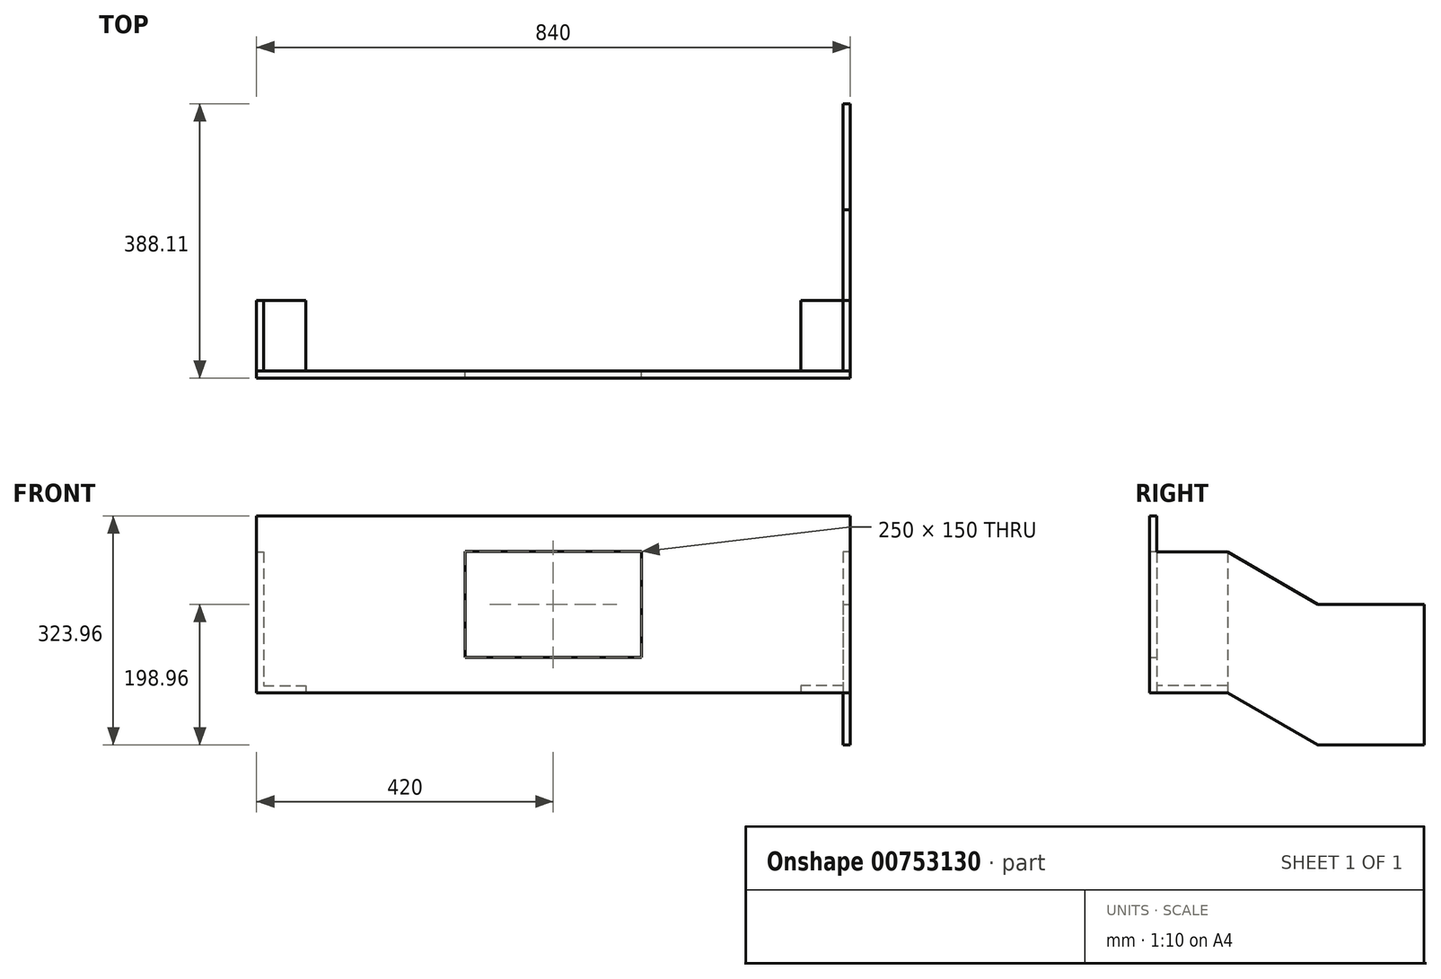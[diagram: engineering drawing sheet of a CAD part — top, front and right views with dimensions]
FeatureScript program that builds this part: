
annotation { "Feature Type Name" : "Feature", "Feature Type Description" : "" }
export const myFeature = defineFeature(function(context is Context, id is Id, definition is map)
    precondition{}
    {
        {
            var Q0;
            Q0=qCreatedBy(makeId("Front.planeOp"),FACE);
            var sketch = newSketch(context, id + "F0", { "sketchPlane" : qUnion([Q0])});
            skLineSegment(sketch, "E0.bottom", {"start": v(-420, 125) * mm, "end": v(420, 125) * mm});
            skLineSegment(sketch, "E0.top", {"start": v(-420, -125) * mm, "end": v(420, -125) * mm});
            skLineSegment(sketch, "E0.left", {"start": v(-420, 125) * mm, "end": v(-420, -125) * mm});
            skLineSegment(sketch, "E0.right", {"start": v(420, 125) * mm, "end": v(420, -125) * mm});
            skPoint(sketch, "E0.middle", {"position": v(0, 0) * mm});
            skLineSegment(sketch, "E1.bottom", {"start": v(-125, 75) * mm, "end": v(125, 75) * mm});
            skLineSegment(sketch, "E1.top", {"start": v(-125, -75) * mm, "end": v(125, -75) * mm});
            skLineSegment(sketch, "E1.left", {"start": v(-125, 75) * mm, "end": v(-125, -75) * mm});
            skLineSegment(sketch, "E1.right", {"start": v(125, 75) * mm, "end": v(125, -75) * mm});
            skSolve(sketch);
        }
        {
            var Q0;
            Q0=makeQuery(id+"F0.imprint","IMPRINT",FACE,{"disambiguationData":[TD([[makeQuery(id+"F0.imprint","IMPRINT",EDGE,{"derivedFrom":sQuery(id+"F0.wireOp",EDGE,"E0.bottom")}),-1.0]])]});
            extrude(context, id + "F1", {"entities" : qUnion([Q0]), "depth" : 10 * mm, "offsetDistance" : 25.4 * mm});
        }
        {
            var Q0;
            Q0=makeQuery(id+"F1.opExtrude","CAP_FACE",FACE,{"disambiguationData":[OSD([sQuery(id+"F0.wireOp",EDGE,"E0.bottom"),sQuery(id+"F0.wireOp",EDGE,"E0.top"),sQuery(id+"F0.wireOp",EDGE,"E0.left"),sQuery(id+"F0.wireOp",EDGE,"E0.right"),sQuery(id+"F0.wireOp",EDGE,"E1.bottom"),sQuery(id+"F0.wireOp",EDGE,"E1.top"),sQuery(id+"F0.wireOp",EDGE,"E1.left"),sQuery(id+"F0.wireOp",EDGE,"E1.right")])],"isStart":true});
            var sketch = newSketch(context, id + "F2", { "sketchPlane" : qUnion([Q0])});
            skLineSegment(sketch, "E2", {"start": v(-410, 73.96) * mm, "end": v(-410, -115) * mm});
            skLineSegment(sketch, "E3", {"start": v(-410, -115) * mm, "end": v(-350, -115) * mm});
            skLineSegment(sketch, "E4", {"start": v(-350, -115) * mm, "end": v(-350, -125) * mm});
            skLineSegment(sketch, "E5", {"start": v(-350, -125) * mm, "end": v(-420, -125) * mm});
            skLineSegment(sketch, "E6", {"start": v(-420, -125) * mm, "end": v(-420, 73.96) * mm});
            skLineSegment(sketch, "E7", {"start": v(-420, 73.96) * mm, "end": v(-410, 73.96) * mm});
            skLineSegment(sketch, "E8", {"start": v(420, 73.96) * mm, "end": v(410, 73.96) * mm});
            skLineSegment(sketch, "E9", {"start": v(410, 73.96) * mm, "end": v(410, -115) * mm});
            skLineSegment(sketch, "E10", {"start": v(410, -115) * mm, "end": v(350, -115) * mm});
            skLineSegment(sketch, "E11", {"start": v(350, -115) * mm, "end": v(350, -125) * mm});
            skLineSegment(sketch, "E12", {"start": v(350, -125) * mm, "end": v(420, -125) * mm});
            skLineSegment(sketch, "E13", {"start": v(420, -125) * mm, "end": v(420, 73.96) * mm});
            skSolve(sketch);
        }
        {
            var Q0;
            Q0=makeQuery(id+"F2.imprint","IMPRINT",FACE,{"disambiguationData":[TD([[makeQuery(id+"F2.imprint","IMPRINT",EDGE,{"derivedFrom":sQuery(id+"F2.wireOp",EDGE,"E8")}),1.0]])]});
            var Q1;
            Q1=makeQuery(id+"F2.imprint","IMPRINT",FACE,{"disambiguationData":[TD([[makeQuery(id+"F2.imprint","IMPRINT",EDGE,{"derivedFrom":sQuery(id+"F2.wireOp",EDGE,"E2")}),-1.0]])]});
            extrude(context, id + "F3", {"entities" : qUnion([Q0, Q1]), "operationType" : NewBodyOperationType.ADD, "depth" : 100 * mm, "offsetDistance" : 25.4 * mm});
        }
        {
            var Q0;
            Q0=makeQuery(id+"F3.boolean.opBoolean","MERGE",FACE,{"derivedFrom":[makeQuery(id+"F1.opExtrude","SWEPT_FACE",FACE,{"disambiguationData":[OSD([sQuery(id+"F0.wireOp",EDGE,"E0.right")])]}),makeQuery(id+"F3.opExtrude","SWEPT_FACE",FACE,{"disambiguationData":[OSD([sQuery(id+"F2.wireOp",EDGE,"E6")])]})]});
            var sketch = newSketch(context, id + "F4", { "sketchPlane" : qUnion([Q0])});
            skLineSegment(sketch, "E14", {"start": v(100, 73.96) * mm, "end": v(228.1, 0) * mm});
            skLineSegment(sketch, "E15", {"start": v(228.1, 0) * mm, "end": v(228.1, -198.96) * mm});
            skLineSegment(sketch, "E16", {"start": v(228.1, -198.96) * mm, "end": v(100, -125) * mm});
            skLineSegment(sketch, "E17", {"start": v(100, -125) * mm, "end": v(100, 73.96) * mm});
            skLineSegment(sketch, "E18", {"start": v(228.1, 0) * mm, "end": v(378.1, 0) * mm});
            skLineSegment(sketch, "E19", {"start": v(378.1, 0) * mm, "end": v(378.1, -198.96) * mm});
            skLineSegment(sketch, "E20", {"start": v(378.1, -198.96) * mm, "end": v(228.1, -198.96) * mm});
            skSolve(sketch);
        }
        {
            var Q0;
            Q0=makeQuery(id+"F4.imprint","IMPRINT",FACE,{"disambiguationData":[TD([[makeQuery(id+"F4.imprint","IMPRINT",EDGE,{"derivedFrom":sQuery(id+"F4.wireOp",EDGE,"E14")}),-1.0]])]});
            var Q1;
            Q1=makeQuery(id+"F4.imprint","IMPRINT",FACE,{"disambiguationData":[TD([[makeQuery(id+"F4.imprint","IMPRINT",EDGE,{"derivedFrom":sQuery(id+"F4.wireOp",EDGE,"E15")}),1.0]])]});
            extrude(context, id + "F5", {"entities" : qUnion([Q0, Q1]), "operationType" : NewBodyOperationType.ADD, "oppositeDirection" : true, "depth" : 10 * mm, "offsetDistance" : 25.4 * mm});
        }
    });
